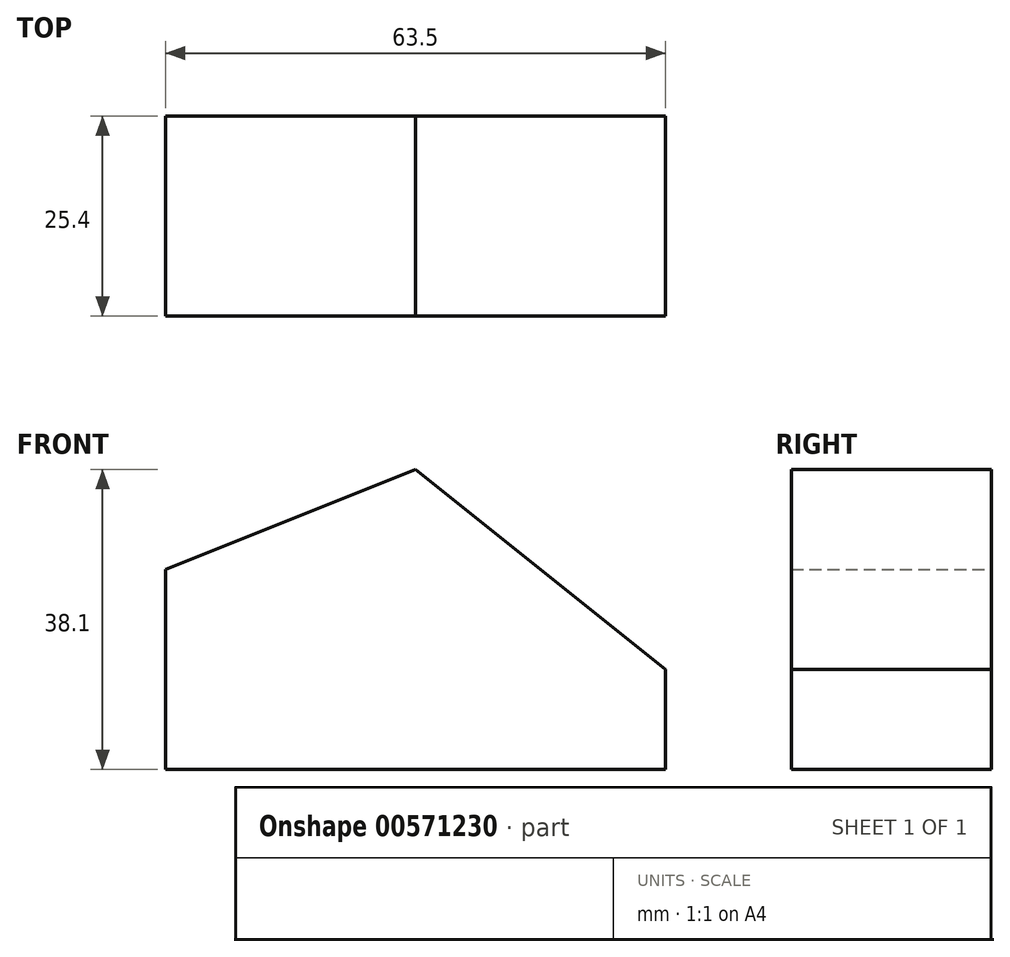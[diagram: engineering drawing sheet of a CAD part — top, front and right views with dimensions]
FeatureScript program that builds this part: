
annotation { "Feature Type Name" : "Feature", "Feature Type Description" : "" }
export const myFeature = defineFeature(function(context is Context, id is Id, definition is map)
    precondition{}
    {
        {
            var Q0;
            Q0=qCreatedBy(makeId("Front.planeOp"),FACE);
            var sketch = newSketch(context, id + "F0", { "sketchPlane" : qUnion([Q0])});
            skLineSegment(sketch, "E0.top", {"start": v(0, 0) * mm, "end": v(63.5, 0) * mm});
            skLineSegment(sketch, "E0.left", {"start": v(0, 25.4) * mm, "end": v(0, 0) * mm});
            skLineSegment(sketch, "E0.right", {"start": v(63.5, 12.7) * mm, "end": v(63.5, 0) * mm});
            skLineSegment(sketch, "E1", {"start": v(0, 25.4) * mm, "end": v(31.75, 38.1) * mm});
            skLineSegment(sketch, "E2", {"start": v(31.75, 38.1) * mm, "end": v(63.5, 12.7) * mm});
            skSolve(sketch);
        }
        {
            var Q0;
            Q0 = qSketchRegion(id + "F0", true);
            extrude(context, id + "F1", {"entities" : qUnion([Q0]), "depth" : 25.4 * mm, "offsetDistance" : 25.4 * mm});
        }
    });
